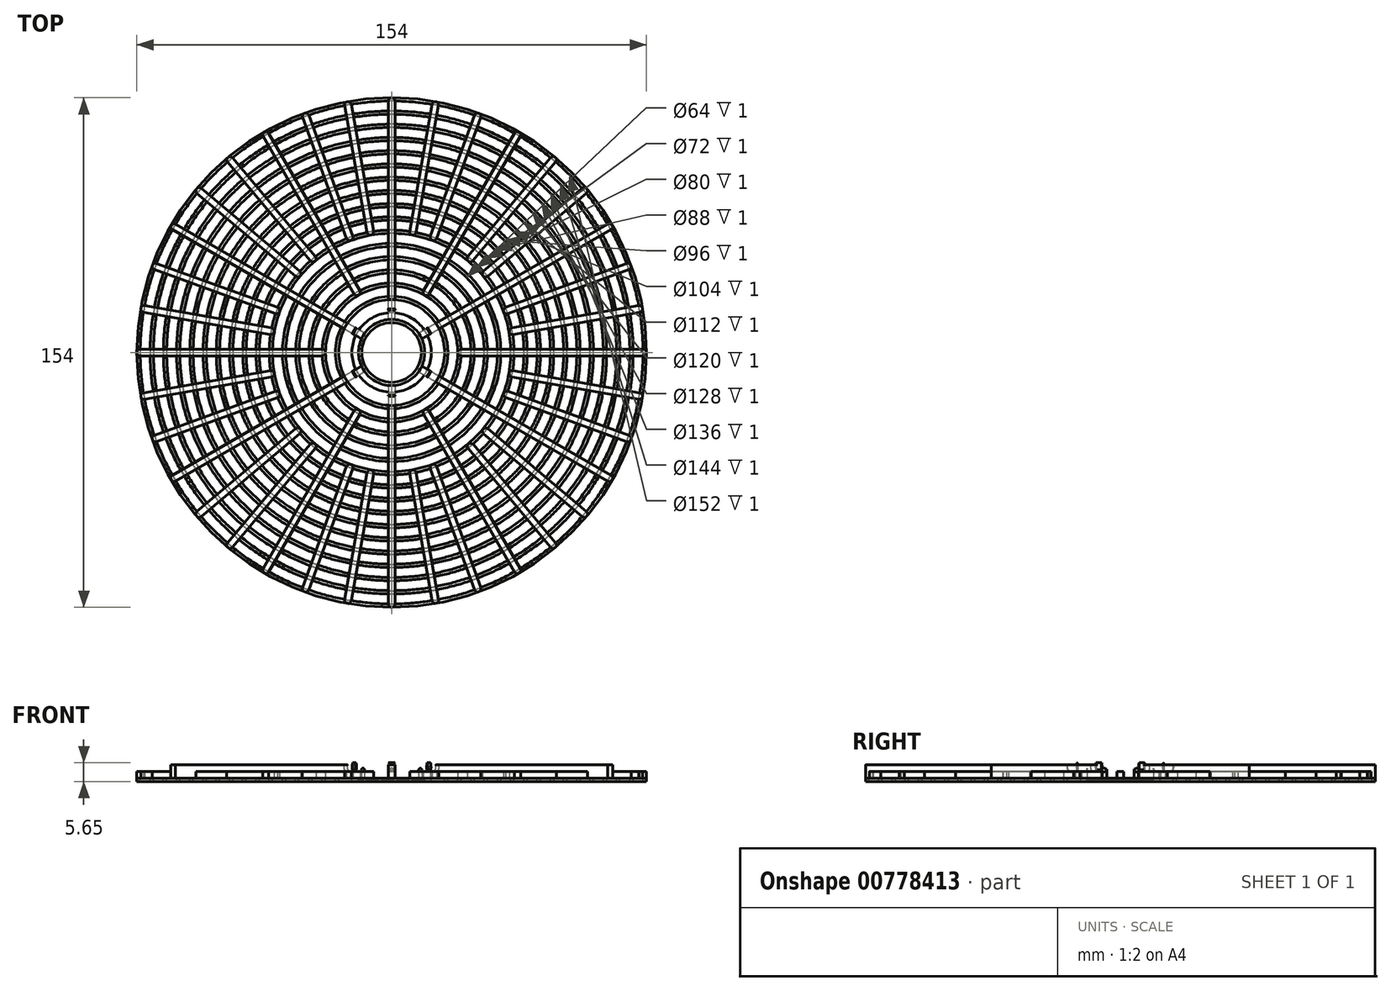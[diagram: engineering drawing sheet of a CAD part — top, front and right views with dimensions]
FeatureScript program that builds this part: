
annotation { "Feature Type Name" : "Feature", "Feature Type Description" : "" }
export const myFeature = defineFeature(function(context is Context, id is Id, definition is map)
    precondition{}
    {
        {
            var Q0;
            Q0=qCreatedBy(makeId("Front.planeOp"),FACE);
            var sketch = newSketch(context, id + "F0", { "sketchPlane" : qUnion([Q0])});
            skLineSegment(sketch, "E0.bottom", {"start": v(16, -1) * mm, "end": v(17, -1) * mm});
            skLineSegment(sketch, "E0.top", {"start": v(16, 0) * mm, "end": v(17, 0) * mm});
            skLineSegment(sketch, "E0.left", {"start": v(16, -1) * mm, "end": v(16, 0) * mm});
            skLineSegment(sketch, "E0.right", {"start": v(17, -1) * mm, "end": v(17, 0) * mm});
            skLineSegment(sketch, "E1.1.0.0", {"start": v(21, -1) * mm, "end": v(21, 0) * mm});
            skLineSegment(sketch, "E1.1.0.1", {"start": v(20, -1) * mm, "end": v(20, 0) * mm});
            skLineSegment(sketch, "E1.1.0.2", {"start": v(20, 0) * mm, "end": v(21, 0) * mm});
            skLineSegment(sketch, "E1.1.0.3", {"start": v(20, -1) * mm, "end": v(21, -1) * mm});
            skLineSegment(sketch, "E1.2.0.0", {"start": v(25, -1) * mm, "end": v(25, 0) * mm});
            skLineSegment(sketch, "E1.2.0.1", {"start": v(24, -1) * mm, "end": v(24, 0) * mm});
            skLineSegment(sketch, "E1.2.0.2", {"start": v(24, 0) * mm, "end": v(25, 0) * mm});
            skLineSegment(sketch, "E1.2.0.3", {"start": v(24, -1) * mm, "end": v(25, -1) * mm});
            skLineSegment(sketch, "E1.3.0.0", {"start": v(29, -1) * mm, "end": v(29, 0) * mm});
            skLineSegment(sketch, "E1.3.0.1", {"start": v(28, -1) * mm, "end": v(28, 0) * mm});
            skLineSegment(sketch, "E1.3.0.2", {"start": v(28, 0) * mm, "end": v(29, 0) * mm});
            skLineSegment(sketch, "E1.3.0.3", {"start": v(28, -1) * mm, "end": v(29, -1) * mm});
            skLineSegment(sketch, "E1.4.0.0", {"start": v(33, -1) * mm, "end": v(33, 0) * mm});
            skLineSegment(sketch, "E1.4.0.1", {"start": v(32, -1) * mm, "end": v(32, 0) * mm});
            skLineSegment(sketch, "E1.4.0.2", {"start": v(32, 0) * mm, "end": v(33, 0) * mm});
            skLineSegment(sketch, "E1.4.0.3", {"start": v(32, -1) * mm, "end": v(33, -1) * mm});
            skLineSegment(sketch, "E1.5.0.0", {"start": v(37, -1) * mm, "end": v(37, 0) * mm});
            skLineSegment(sketch, "E1.5.0.1", {"start": v(36, -1) * mm, "end": v(36, 0) * mm});
            skLineSegment(sketch, "E1.5.0.2", {"start": v(36, 0) * mm, "end": v(37, 0) * mm});
            skLineSegment(sketch, "E1.5.0.3", {"start": v(36, -1) * mm, "end": v(37, -1) * mm});
            skLineSegment(sketch, "E1.6.0.0", {"start": v(41, -1) * mm, "end": v(41, 0) * mm});
            skLineSegment(sketch, "E1.6.0.1", {"start": v(40, -1) * mm, "end": v(40, 0) * mm});
            skLineSegment(sketch, "E1.6.0.2", {"start": v(40, 0) * mm, "end": v(41, 0) * mm});
            skLineSegment(sketch, "E1.6.0.3", {"start": v(40, -1) * mm, "end": v(41, -1) * mm});
            skLineSegment(sketch, "E1.7.0.0", {"start": v(45, -1) * mm, "end": v(45, 0) * mm});
            skLineSegment(sketch, "E1.7.0.1", {"start": v(44, -1) * mm, "end": v(44, 0) * mm});
            skLineSegment(sketch, "E1.7.0.2", {"start": v(44, 0) * mm, "end": v(45, 0) * mm});
            skLineSegment(sketch, "E1.7.0.3", {"start": v(44, -1) * mm, "end": v(45, -1) * mm});
            skLineSegment(sketch, "E1.8.0.0", {"start": v(49, -1) * mm, "end": v(49, 0) * mm});
            skLineSegment(sketch, "E1.8.0.1", {"start": v(48, -1) * mm, "end": v(48, 0) * mm});
            skLineSegment(sketch, "E1.8.0.2", {"start": v(48, 0) * mm, "end": v(49, 0) * mm});
            skLineSegment(sketch, "E1.8.0.3", {"start": v(48, -1) * mm, "end": v(49, -1) * mm});
            skLineSegment(sketch, "E1.9.0.0", {"start": v(53, -1) * mm, "end": v(53, 0) * mm});
            skLineSegment(sketch, "E1.9.0.1", {"start": v(52, -1) * mm, "end": v(52, 0) * mm});
            skLineSegment(sketch, "E1.9.0.2", {"start": v(52, 0) * mm, "end": v(53, 0) * mm});
            skLineSegment(sketch, "E1.9.0.3", {"start": v(52, -1) * mm, "end": v(53, -1) * mm});
            skLineSegment(sketch, "E1.10.0.0", {"start": v(57, -1) * mm, "end": v(57, 0) * mm});
            skLineSegment(sketch, "E1.10.0.1", {"start": v(56, -1) * mm, "end": v(56, 0) * mm});
            skLineSegment(sketch, "E1.10.0.2", {"start": v(56, 0) * mm, "end": v(57, 0) * mm});
            skLineSegment(sketch, "E1.10.0.3", {"start": v(56, -1) * mm, "end": v(57, -1) * mm});
            skLineSegment(sketch, "E1.11.0.0", {"start": v(61, -1) * mm, "end": v(61, 0) * mm});
            skLineSegment(sketch, "E1.11.0.1", {"start": v(60, -1) * mm, "end": v(60, 0) * mm});
            skLineSegment(sketch, "E1.11.0.2", {"start": v(60, 0) * mm, "end": v(61, 0) * mm});
            skLineSegment(sketch, "E1.11.0.3", {"start": v(60, -1) * mm, "end": v(61, -1) * mm});
            skLineSegment(sketch, "E1.12.0.0", {"start": v(65, -1) * mm, "end": v(65, 0) * mm});
            skLineSegment(sketch, "E1.12.0.1", {"start": v(64, -1) * mm, "end": v(64, 0) * mm});
            skLineSegment(sketch, "E1.12.0.2", {"start": v(64, 0) * mm, "end": v(65, 0) * mm});
            skLineSegment(sketch, "E1.12.0.3", {"start": v(64, -1) * mm, "end": v(65, -1) * mm});
            skLineSegment(sketch, "E1.13.0.0", {"start": v(69, -1) * mm, "end": v(69, 0) * mm});
            skLineSegment(sketch, "E1.13.0.1", {"start": v(68, -1) * mm, "end": v(68, 0) * mm});
            skLineSegment(sketch, "E1.13.0.2", {"start": v(68, 0) * mm, "end": v(69, 0) * mm});
            skLineSegment(sketch, "E1.13.0.3", {"start": v(68, -1) * mm, "end": v(69, -1) * mm});
            skLineSegment(sketch, "E1.14.0.0", {"start": v(73, -1) * mm, "end": v(73, 0) * mm});
            skLineSegment(sketch, "E1.14.0.1", {"start": v(72, -1) * mm, "end": v(72, 0) * mm});
            skLineSegment(sketch, "E1.14.0.2", {"start": v(72, 0) * mm, "end": v(73, 0) * mm});
            skLineSegment(sketch, "E1.14.0.3", {"start": v(72, -1) * mm, "end": v(73, -1) * mm});
            skLineSegment(sketch, "E1.15.0.0", {"start": v(77, -1) * mm, "end": v(77, 0) * mm});
            skLineSegment(sketch, "E1.15.0.1", {"start": v(76, -1) * mm, "end": v(76, 0) * mm});
            skLineSegment(sketch, "E1.15.0.2", {"start": v(76, 0) * mm, "end": v(77, 0) * mm});
            skLineSegment(sketch, "E1.15.0.3", {"start": v(76, -1) * mm, "end": v(77, -1) * mm});
            skLineSegment(sketch, "E1.direction1", {"start": v(16, -1) * mm, "end": v(20, -1) * mm, "construction": true});
            skLineSegment(sketch, "E2", {"start": v(0, 44.74) * mm, "end": v(0, -46.31) * mm, "construction": true});
            skLineSegment(sketch, "E3", {"start": v(-40.31, 0) * mm, "end": v(86.53, 0) * mm, "construction": true});
            skLineSegment(sketch, "E4.bottom", {"start": v(0, -1) * mm, "end": v(12, -1) * mm});
            skLineSegment(sketch, "E4.top", {"start": v(0, 0) * mm, "end": v(9, 0) * mm});
            skLineSegment(sketch, "E4.left", {"start": v(0, -1) * mm, "end": v(0, 0) * mm});
            skLineSegment(sketch, "E4.right", {"start": v(12, -1) * mm, "end": v(12, 0) * mm});
            skLineSegment(sketch, "E5.top", {"start": v(9, -0.6) * mm, "end": v(10, -0.6) * mm});
            skLineSegment(sketch, "E5.left", {"start": v(9, 0) * mm, "end": v(9, -0.6) * mm});
            skLineSegment(sketch, "E5.right", {"start": v(10, 0) * mm, "end": v(10, -0.6) * mm});
            skLineSegment(sketch, "E6.trimOffspring", {"start": v(10, 0) * mm, "end": v(12, 0) * mm});
            skSolve(sketch);
        }
        {
            var Q0;
            Q0=makeQuery(id+"F0.imprint","IMPRINT",FACE,{"disambiguationData":[TD([[makeQuery(id+"F0.imprint","IMPRINT",EDGE,{"derivedFrom":sQuery(id+"F0.wireOp",EDGE,"E1.15.0.0")}),1.0]])]});
            var Q1;
            Q1=makeQuery(id+"F0.imprint","IMPRINT",FACE,{"disambiguationData":[TD([[makeQuery(id+"F0.imprint","IMPRINT",EDGE,{"derivedFrom":sQuery(id+"F0.wireOp",EDGE,"E1.13.0.0")}),1.0]])]});
            var Q2;
            Q2=makeQuery(id+"F0.imprint","IMPRINT",FACE,{"disambiguationData":[TD([[makeQuery(id+"F0.imprint","IMPRINT",EDGE,{"derivedFrom":sQuery(id+"F0.wireOp",EDGE,"E1.14.0.0")}),1.0]])]});
            var Q3;
            Q3=makeQuery(id+"F0.imprint","IMPRINT",FACE,{"disambiguationData":[TD([[makeQuery(id+"F0.imprint","IMPRINT",EDGE,{"derivedFrom":sQuery(id+"F0.wireOp",EDGE,"E1.3.0.0")}),1.0]])]});
            var Q4;
            Q4=makeQuery(id+"F0.imprint","IMPRINT",FACE,{"disambiguationData":[TD([[makeQuery(id+"F0.imprint","IMPRINT",EDGE,{"derivedFrom":sQuery(id+"F0.wireOp",EDGE,"E1.4.0.0")}),1.0]])]});
            var Q5;
            Q5=makeQuery(id+"F0.imprint","IMPRINT",FACE,{"disambiguationData":[TD([[makeQuery(id+"F0.imprint","IMPRINT",EDGE,{"derivedFrom":sQuery(id+"F0.wireOp",EDGE,"E1.5.0.0")}),1.0]])]});
            var Q6;
            Q6=makeQuery(id+"F0.imprint","IMPRINT",FACE,{"disambiguationData":[TD([[makeQuery(id+"F0.imprint","IMPRINT",EDGE,{"derivedFrom":sQuery(id+"F0.wireOp",EDGE,"E1.7.0.0")}),1.0]])]});
            var Q7;
            Q7=makeQuery(id+"F0.imprint","IMPRINT",FACE,{"disambiguationData":[TD([[makeQuery(id+"F0.imprint","IMPRINT",EDGE,{"derivedFrom":sQuery(id+"F0.wireOp",EDGE,"E1.6.0.0")}),1.0]])]});
            var Q8;
            Q8=makeQuery(id+"F0.imprint","IMPRINT",FACE,{"disambiguationData":[TD([[makeQuery(id+"F0.imprint","IMPRINT",EDGE,{"derivedFrom":sQuery(id+"F0.wireOp",EDGE,"E1.2.0.0")}),1.0]])]});
            var Q9;
            Q9=makeQuery(id+"F0.imprint","IMPRINT",FACE,{"disambiguationData":[TD([[makeQuery(id+"F0.imprint","IMPRINT",EDGE,{"derivedFrom":sQuery(id+"F0.wireOp",EDGE,"E1.8.0.0")}),1.0]])]});
            var Q10;
            Q10=makeQuery(id+"F0.imprint","IMPRINT",FACE,{"disambiguationData":[TD([[makeQuery(id+"F0.imprint","IMPRINT",EDGE,{"derivedFrom":sQuery(id+"F0.wireOp",EDGE,"E1.9.0.0")}),1.0]])]});
            var Q11;
            Q11=makeQuery(id+"F0.imprint","IMPRINT",FACE,{"disambiguationData":[TD([[makeQuery(id+"F0.imprint","IMPRINT",EDGE,{"derivedFrom":sQuery(id+"F0.wireOp",EDGE,"E1.10.0.0")}),1.0]])]});
            var Q12;
            Q12=makeQuery(id+"F0.imprint","IMPRINT",FACE,{"disambiguationData":[TD([[makeQuery(id+"F0.imprint","IMPRINT",EDGE,{"derivedFrom":sQuery(id+"F0.wireOp",EDGE,"E1.11.0.0")}),1.0]])]});
            var Q13;
            Q13=makeQuery(id+"F0.imprint","IMPRINT",FACE,{"disambiguationData":[TD([[makeQuery(id+"F0.imprint","IMPRINT",EDGE,{"derivedFrom":sQuery(id+"F0.wireOp",EDGE,"E1.12.0.0")}),1.0]])]});
            var Q14;
            Q14=makeQuery(id+"F0.imprint","IMPRINT",FACE,{"disambiguationData":[TD([[makeQuery(id+"F0.imprint","IMPRINT",EDGE,{"derivedFrom":sQuery(id+"F0.wireOp",EDGE,"E0.bottom")}),1.0]])]});
            var Q15;
            Q15=makeQuery(id+"F0.imprint","IMPRINT",FACE,{"disambiguationData":[TD([[makeQuery(id+"F0.imprint","IMPRINT",EDGE,{"derivedFrom":sQuery(id+"F0.wireOp",EDGE,"E1.1.0.0")}),1.0]])]});
            var Q16;
            Q16=makeQuery(id+"F0.imprint","IMPRINT",FACE,{"disambiguationData":[TD([[makeQuery(id+"F0.imprint","IMPRINT",EDGE,{"derivedFrom":sQuery(id+"F0.wireOp",EDGE,"E4.bottom")}),1.0]])]});
            var Q17;
            Q17=sQuery(id+"F0.wireOp",EDGE,"E2");
            revolve(context, id + "F1", {"surfaceOperationType" : NewSurfaceOperationType.NEW, "entities" : qUnion([Q0, Q1, Q2, Q3, Q4, Q5, Q6, Q7, Q8, Q9, Q10, Q11, Q12, Q13, Q14, Q15, Q16]), "axis" : qUnion([Q17]), "revolveType" : RevolveType.FULL});
        }
        {
            var Q0;
            Q0=qCreatedBy(makeId("Top.planeOp"),FACE);
            var sketch = newSketch(context, id + "F2", { "sketchPlane" : qUnion([Q0])});
            skLineSegment(sketch, "E7.top", {"start": v(1, -10) * mm, "end": v(-1, -10) * mm});
            skLineSegment(sketch, "E7.left", {"start": v(1, -76) * mm, "end": v(1, -10) * mm});
            skLineSegment(sketch, "E7.right", {"start": v(-1, -76) * mm, "end": v(-1, -10) * mm});
            skPoint(sketch, "E7.middle", {"position": v(0, -28.84) * mm});
            skArc(sketch, "E8", {"start": v(-1, -76) * mm, "mid": v(0, -77) * mm, "end": v(1, -76) * mm});
            skLineSegment(sketch, "E9.1.0", {"start": v(65.32, -38.87) * mm, "end": v(8.16, -5.87) * mm});
            skLineSegment(sketch, "E9.1.1", {"start": v(66.32, -37.13) * mm, "end": v(9.16, -4.13) * mm});
            skPoint(sketch, "E9.1.2", {"position": v(24.97, -14.42) * mm});
            skLineSegment(sketch, "E9.1.3", {"start": v(9.16, -4.13) * mm, "end": v(8.16, -5.87) * mm});
            skArc(sketch, "E9.1.4", {"start": v(65.32, -38.87) * mm, "mid": v(66.68, -38.5) * mm, "end": v(66.32, -37.13) * mm});
            skLineSegment(sketch, "E9.2.0", {"start": v(66.32, 37.13) * mm, "end": v(9.16, 4.13) * mm});
            skLineSegment(sketch, "E9.2.1", {"start": v(65.32, 38.87) * mm, "end": v(8.16, 5.87) * mm});
            skPoint(sketch, "E9.2.2", {"position": v(24.97, 14.42) * mm});
            skLineSegment(sketch, "E9.2.3", {"start": v(8.16, 5.87) * mm, "end": v(9.16, 4.13) * mm});
            skArc(sketch, "E9.2.4", {"start": v(66.32, 37.13) * mm, "mid": v(66.68, 38.5) * mm, "end": v(65.32, 38.87) * mm});
            skLineSegment(sketch, "E9.3.0", {"start": v(1, 76) * mm, "end": v(1, 10) * mm});
            skLineSegment(sketch, "E9.3.1", {"start": v(-1, 76) * mm, "end": v(-1, 10) * mm});
            skPoint(sketch, "E9.3.2", {"position": v(0, 28.84) * mm});
            skLineSegment(sketch, "E9.3.3", {"start": v(-1, 10) * mm, "end": v(1, 10) * mm});
            skArc(sketch, "E9.3.4", {"start": v(1, 76) * mm, "mid": v(0, 77) * mm, "end": v(-1, 76) * mm});
            skPoint(sketch, "E9.center", {"position": v(0, 0) * mm});
            skLineSegment(sketch, "E10.1.4.0", {"start": v(-65.32, 38.87) * mm, "end": v(-8.16, 5.87) * mm});
            skLineSegment(sketch, "E10.3.4.0", {"start": v(-66.32, 37.13) * mm, "end": v(-9.16, 4.13) * mm});
            skPoint(sketch, "E10.6.4.0", {"position": v(-24.97, 14.42) * mm});
            skLineSegment(sketch, "E10.7.4.0", {"start": v(-9.16, 4.13) * mm, "end": v(-8.16, 5.87) * mm});
            skArc(sketch, "E10.10.4.0", {"start": v(-65.32, 38.87) * mm, "mid": v(-66.68, 38.5) * mm, "end": v(-66.32, 37.13) * mm});
            skLineSegment(sketch, "E10.1.5.0", {"start": v(-66.32, -37.13) * mm, "end": v(-9.16, -4.13) * mm});
            skLineSegment(sketch, "E10.3.5.0", {"start": v(-65.32, -38.87) * mm, "end": v(-8.16, -5.87) * mm});
            skPoint(sketch, "E10.6.5.0", {"position": v(-24.97, -14.42) * mm});
            skLineSegment(sketch, "E10.7.5.0", {"start": v(-8.16, -5.87) * mm, "end": v(-9.16, -4.13) * mm});
            skArc(sketch, "E10.10.5.0", {"start": v(-66.32, -37.13) * mm, "mid": v(-66.68, -38.5) * mm, "end": v(-65.32, -38.87) * mm});
            skSolve(sketch);
        }
        {
            var Q0;
            Q0 = qSketchRegion(id + "F2", true);
            extrude(context, id + "F3", {"entities" : qUnion([Q0]), "depth" : 4 * mm, "offsetDistance" : 25 * mm});
        }
        {
            var Q0;
            Q0=qCreatedBy(makeId("Top.planeOp"),FACE);
            var sketch = newSketch(context, id + "F4", { "sketchPlane" : qUnion([Q0])});
            skArc(sketch, "E11", {"start": v(-76, 1) * mm, "mid": v(-77, 0) * mm, "end": v(-76, -1) * mm});
            skArc(sketch, "E12", {"start": v(-21.01, -1) * mm, "mid": v(-20.01, 0) * mm, "end": v(-21.01, 1) * mm});
            skLineSegment(sketch, "E13", {"start": v(-76, -1) * mm, "end": v(-21.01, -1) * mm});
            skLineSegment(sketch, "E14", {"start": v(-21.01, 1) * mm, "end": v(-76, 1) * mm});
            skArc(sketch, "E15.1.0", {"start": v(-38.86, -65.3) * mm, "mid": v(-38.5, -66.68) * mm, "end": v(-37.13, -66.3) * mm});
            skLineSegment(sketch, "E15.1.1", {"start": v(-37.13, -66.3) * mm, "end": v(-9.64, -18.7) * mm});
            skLineSegment(sketch, "E15.1.2", {"start": v(-11.37, -17.7) * mm, "end": v(-38.86, -65.3) * mm});
            skArc(sketch, "E15.1.3", {"start": v(-9.64, -18.7) * mm, "mid": v(-10, -17.33) * mm, "end": v(-11.37, -17.7) * mm});
            skArc(sketch, "E15.2.0", {"start": v(37.13, -66.3) * mm, "mid": v(38.5, -66.68) * mm, "end": v(38.86, -65.3) * mm});
            skLineSegment(sketch, "E15.2.1", {"start": v(38.86, -65.3) * mm, "end": v(11.37, -17.7) * mm});
            skLineSegment(sketch, "E15.2.2", {"start": v(9.64, -18.7) * mm, "end": v(37.13, -66.3) * mm});
            skArc(sketch, "E15.2.3", {"start": v(11.37, -17.7) * mm, "mid": v(10, -17.33) * mm, "end": v(9.64, -18.7) * mm});
            skArc(sketch, "E15.3.0", {"start": v(76, -1) * mm, "mid": v(77, 0) * mm, "end": v(76, 1) * mm});
            skLineSegment(sketch, "E15.3.1", {"start": v(76, 1) * mm, "end": v(21.01, 1) * mm});
            skLineSegment(sketch, "E15.3.2", {"start": v(21.01, -1) * mm, "end": v(76, -1) * mm});
            skArc(sketch, "E15.3.3", {"start": v(21.01, 1) * mm, "mid": v(20.01, 0) * mm, "end": v(21.01, -1) * mm});
            skArc(sketch, "E15.4.0", {"start": v(38.86, 65.3) * mm, "mid": v(38.5, 66.68) * mm, "end": v(37.13, 66.3) * mm});
            skLineSegment(sketch, "E15.4.1", {"start": v(37.13, 66.3) * mm, "end": v(9.64, 18.7) * mm});
            skLineSegment(sketch, "E15.4.2", {"start": v(11.37, 17.7) * mm, "end": v(38.86, 65.3) * mm});
            skArc(sketch, "E15.4.3", {"start": v(9.64, 18.7) * mm, "mid": v(10, 17.33) * mm, "end": v(11.37, 17.7) * mm});
            skArc(sketch, "E15.5.0", {"start": v(-37.13, 66.3) * mm, "mid": v(-38.5, 66.68) * mm, "end": v(-38.86, 65.3) * mm});
            skLineSegment(sketch, "E15.5.1", {"start": v(-38.86, 65.3) * mm, "end": v(-11.37, 17.7) * mm});
            skLineSegment(sketch, "E15.5.2", {"start": v(-9.64, 18.7) * mm, "end": v(-37.13, 66.3) * mm});
            skArc(sketch, "E15.5.3", {"start": v(-11.37, 17.7) * mm, "mid": v(-10, 17.33) * mm, "end": v(-9.64, 18.7) * mm});
            skPoint(sketch, "E15.center", {"position": v(0, 0) * mm});
            skSolve(sketch);
        }
        {
            var Q0;
            Q0 = qSketchRegion(id + "F4", true);
            extrude(context, id + "F5", {"entities" : qUnion([Q0]), "operationType" : NewBodyOperationType.ADD, "depth" : 2 * mm, "offsetDistance" : 25 * mm});
        }
        {
            var Q0;
            Q0=qCreatedBy(makeId("Top.planeOp"),FACE);
            var sketch = newSketch(context, id + "F6", { "sketchPlane" : qUnion([Q0])});
            skLineSegment(sketch, "E16", {"start": v(0, 0) * mm, "end": v(-85.94, -31.28) * mm, "construction": true});
            skLineSegment(sketch, "E17", {"start": v(0, 0) * mm, "end": v(-88.81, -15.66) * mm, "construction": true});
            skSolve(sketch);
        }
        {
            var Q0;
            Q0=qCreatedBy(makeId("Top.planeOp"),FACE);
            var sketch = newSketch(context, id + "F7", { "sketchPlane" : qUnion([Q0])});
            skArc(sketch, "E18", {"start": v(-74.99, -12.2) * mm, "mid": v(-75.8, -13.37) * mm, "end": v(-74.64, -14.18) * mm});
            skArc(sketch, "E19", {"start": v(-71.73, -25.04) * mm, "mid": v(-72.33, -26.33) * mm, "end": v(-71.05, -26.92) * mm});
            skArc(sketch, "E20", {"start": v(-34.5, -13.62) * mm, "mid": v(-33.91, -12.34) * mm, "end": v(-35.2, -11.74) * mm});
            skArc(sketch, "E21", {"start": v(-36.36, -7.43) * mm, "mid": v(-35.55, -6.27) * mm, "end": v(-36.7, -5.46) * mm});
            skLineSegment(sketch, "E22", {"start": v(-71.05, -26.92) * mm, "end": v(-34.5, -13.62) * mm});
            skLineSegment(sketch, "E23", {"start": v(-35.2, -11.74) * mm, "end": v(-71.73, -25.04) * mm});
            skLineSegment(sketch, "E24", {"start": v(-74.64, -14.18) * mm, "end": v(-36.36, -7.43) * mm});
            skLineSegment(sketch, "E25", {"start": v(-36.7, -5.46) * mm, "end": v(-74.99, -12.2) * mm});
            skLineSegment(sketch, "E26.1.0", {"start": v(-29.06, -23.08) * mm, "end": v(-58.84, -48.07) * mm});
            skArc(sketch, "E26.1.1", {"start": v(-58.84, -48.07) * mm, "mid": v(-58.96, -49.47) * mm, "end": v(-57.55, -49.6) * mm});
            skLineSegment(sketch, "E26.1.2", {"start": v(-57.55, -49.6) * mm, "end": v(-27.78, -24.61) * mm});
            skLineSegment(sketch, "E26.1.3", {"start": v(-24.6, -27.77) * mm, "end": v(-49.6, -57.56) * mm});
            skLineSegment(sketch, "E26.1.4", {"start": v(-48.07, -58.84) * mm, "end": v(-23.07, -29.05) * mm});
            skArc(sketch, "E26.1.5", {"start": v(-49.6, -57.56) * mm, "mid": v(-49.48, -58.97) * mm, "end": v(-48.07, -58.84) * mm});
            skArc(sketch, "E26.1.6", {"start": v(-27.78, -24.61) * mm, "mid": v(-27.65, -23.2) * mm, "end": v(-29.06, -23.08) * mm});
            skArc(sketch, "E26.1.7", {"start": v(-23.07, -29.05) * mm, "mid": v(-23.2, -27.64) * mm, "end": v(-24.6, -27.77) * mm});
            skLineSegment(sketch, "E26.2.0", {"start": v(-13.63, -34.52) * mm, "end": v(-26.92, -71.04) * mm});
            skArc(sketch, "E26.2.1", {"start": v(-26.92, -71.04) * mm, "mid": v(-26.32, -72.33) * mm, "end": v(-25.04, -71.73) * mm});
            skLineSegment(sketch, "E26.2.2", {"start": v(-25.04, -71.73) * mm, "end": v(-11.75, -35.2) * mm});
            skLineSegment(sketch, "E26.2.3", {"start": v(-7.42, -36.35) * mm, "end": v(-14.18, -74.65) * mm});
            skLineSegment(sketch, "E26.2.4", {"start": v(-12.2, -75) * mm, "end": v(-5.46, -36.7) * mm});
            skArc(sketch, "E26.2.5", {"start": v(-14.18, -74.65) * mm, "mid": v(-13.37, -75.8) * mm, "end": v(-12.2, -75) * mm});
            skArc(sketch, "E26.2.6", {"start": v(-11.75, -35.2) * mm, "mid": v(-12.35, -33.92) * mm, "end": v(-13.63, -34.52) * mm});
            skArc(sketch, "E26.2.7", {"start": v(-5.46, -36.7) * mm, "mid": v(-6.27, -35.54) * mm, "end": v(-7.42, -36.35) * mm});
            skLineSegment(sketch, "E26.3.0", {"start": v(5.46, -36.7) * mm, "end": v(12.2, -74.99) * mm});
            skArc(sketch, "E26.3.1", {"start": v(12.2, -74.99) * mm, "mid": v(13.37, -75.8) * mm, "end": v(14.18, -74.64) * mm});
            skLineSegment(sketch, "E26.3.2", {"start": v(14.18, -74.64) * mm, "end": v(7.43, -36.36) * mm});
            skLineSegment(sketch, "E26.3.3", {"start": v(11.74, -35.2) * mm, "end": v(25.04, -71.73) * mm});
            skLineSegment(sketch, "E26.3.4", {"start": v(26.92, -71.05) * mm, "end": v(13.62, -34.5) * mm});
            skArc(sketch, "E26.3.5", {"start": v(25.04, -71.73) * mm, "mid": v(26.33, -72.33) * mm, "end": v(26.92, -71.05) * mm});
            skArc(sketch, "E26.3.6", {"start": v(7.43, -36.36) * mm, "mid": v(6.27, -35.55) * mm, "end": v(5.46, -36.7) * mm});
            skArc(sketch, "E26.3.7", {"start": v(13.62, -34.5) * mm, "mid": v(12.34, -33.91) * mm, "end": v(11.74, -35.2) * mm});
            skLineSegment(sketch, "E26.4.0", {"start": v(23.08, -29.06) * mm, "end": v(48.07, -58.84) * mm});
            skArc(sketch, "E26.4.1", {"start": v(48.07, -58.84) * mm, "mid": v(49.47, -58.96) * mm, "end": v(49.6, -57.55) * mm});
            skLineSegment(sketch, "E26.4.2", {"start": v(49.6, -57.55) * mm, "end": v(24.61, -27.78) * mm});
            skLineSegment(sketch, "E26.4.3", {"start": v(27.77, -24.6) * mm, "end": v(57.56, -49.6) * mm});
            skLineSegment(sketch, "E26.4.4", {"start": v(58.84, -48.07) * mm, "end": v(29.05, -23.07) * mm});
            skArc(sketch, "E26.4.5", {"start": v(57.56, -49.6) * mm, "mid": v(58.97, -49.48) * mm, "end": v(58.84, -48.07) * mm});
            skArc(sketch, "E26.4.6", {"start": v(24.61, -27.78) * mm, "mid": v(23.2, -27.65) * mm, "end": v(23.08, -29.06) * mm});
            skArc(sketch, "E26.4.7", {"start": v(29.05, -23.07) * mm, "mid": v(27.64, -23.2) * mm, "end": v(27.77, -24.6) * mm});
            skLineSegment(sketch, "E26.5.0", {"start": v(34.52, -13.63) * mm, "end": v(71.04, -26.92) * mm});
            skArc(sketch, "E26.5.1", {"start": v(71.04, -26.92) * mm, "mid": v(72.33, -26.32) * mm, "end": v(71.73, -25.04) * mm});
            skLineSegment(sketch, "E26.5.2", {"start": v(71.73, -25.04) * mm, "end": v(35.2, -11.75) * mm});
            skLineSegment(sketch, "E26.5.3", {"start": v(36.35, -7.42) * mm, "end": v(74.65, -14.18) * mm});
            skLineSegment(sketch, "E26.5.4", {"start": v(75, -12.2) * mm, "end": v(36.7, -5.46) * mm});
            skArc(sketch, "E26.5.5", {"start": v(74.65, -14.18) * mm, "mid": v(75.8, -13.37) * mm, "end": v(75, -12.2) * mm});
            skArc(sketch, "E26.5.6", {"start": v(35.2, -11.75) * mm, "mid": v(33.92, -12.35) * mm, "end": v(34.52, -13.63) * mm});
            skArc(sketch, "E26.5.7", {"start": v(36.7, -5.46) * mm, "mid": v(35.54, -6.27) * mm, "end": v(36.35, -7.42) * mm});
            skLineSegment(sketch, "E26.6.0", {"start": v(36.7, 5.46) * mm, "end": v(74.99, 12.2) * mm});
            skArc(sketch, "E26.6.1", {"start": v(74.99, 12.2) * mm, "mid": v(75.8, 13.37) * mm, "end": v(74.64, 14.18) * mm});
            skLineSegment(sketch, "E26.6.2", {"start": v(74.64, 14.18) * mm, "end": v(36.36, 7.43) * mm});
            skLineSegment(sketch, "E26.6.3", {"start": v(35.2, 11.74) * mm, "end": v(71.73, 25.04) * mm});
            skLineSegment(sketch, "E26.6.4", {"start": v(71.05, 26.92) * mm, "end": v(34.5, 13.62) * mm});
            skArc(sketch, "E26.6.5", {"start": v(71.73, 25.04) * mm, "mid": v(72.33, 26.33) * mm, "end": v(71.05, 26.92) * mm});
            skArc(sketch, "E26.6.6", {"start": v(36.36, 7.43) * mm, "mid": v(35.55, 6.27) * mm, "end": v(36.7, 5.46) * mm});
            skArc(sketch, "E26.6.7", {"start": v(34.5, 13.62) * mm, "mid": v(33.91, 12.34) * mm, "end": v(35.2, 11.74) * mm});
            skLineSegment(sketch, "E26.7.0", {"start": v(29.06, 23.08) * mm, "end": v(58.84, 48.07) * mm});
            skArc(sketch, "E26.7.1", {"start": v(58.84, 48.07) * mm, "mid": v(58.96, 49.47) * mm, "end": v(57.55, 49.6) * mm});
            skLineSegment(sketch, "E26.7.2", {"start": v(57.55, 49.6) * mm, "end": v(27.78, 24.61) * mm});
            skLineSegment(sketch, "E26.7.3", {"start": v(24.6, 27.77) * mm, "end": v(49.6, 57.56) * mm});
            skLineSegment(sketch, "E26.7.4", {"start": v(48.07, 58.84) * mm, "end": v(23.07, 29.05) * mm});
            skArc(sketch, "E26.7.5", {"start": v(49.6, 57.56) * mm, "mid": v(49.48, 58.97) * mm, "end": v(48.07, 58.84) * mm});
            skArc(sketch, "E26.7.6", {"start": v(27.78, 24.61) * mm, "mid": v(27.65, 23.2) * mm, "end": v(29.06, 23.08) * mm});
            skArc(sketch, "E26.7.7", {"start": v(23.07, 29.05) * mm, "mid": v(23.2, 27.64) * mm, "end": v(24.6, 27.77) * mm});
            skLineSegment(sketch, "E26.8.0", {"start": v(13.63, 34.52) * mm, "end": v(26.92, 71.04) * mm});
            skArc(sketch, "E26.8.1", {"start": v(26.92, 71.04) * mm, "mid": v(26.32, 72.33) * mm, "end": v(25.04, 71.73) * mm});
            skLineSegment(sketch, "E26.8.2", {"start": v(25.04, 71.73) * mm, "end": v(11.75, 35.2) * mm});
            skLineSegment(sketch, "E26.8.3", {"start": v(7.42, 36.35) * mm, "end": v(14.18, 74.65) * mm});
            skLineSegment(sketch, "E26.8.4", {"start": v(12.2, 75) * mm, "end": v(5.46, 36.7) * mm});
            skArc(sketch, "E26.8.5", {"start": v(14.18, 74.65) * mm, "mid": v(13.37, 75.8) * mm, "end": v(12.2, 75) * mm});
            skArc(sketch, "E26.8.6", {"start": v(11.75, 35.2) * mm, "mid": v(12.35, 33.92) * mm, "end": v(13.63, 34.52) * mm});
            skArc(sketch, "E26.8.7", {"start": v(5.46, 36.7) * mm, "mid": v(6.27, 35.54) * mm, "end": v(7.42, 36.35) * mm});
            skLineSegment(sketch, "E26.9.0", {"start": v(-5.46, 36.7) * mm, "end": v(-12.2, 74.99) * mm});
            skArc(sketch, "E26.9.1", {"start": v(-12.2, 74.99) * mm, "mid": v(-13.37, 75.8) * mm, "end": v(-14.18, 74.64) * mm});
            skLineSegment(sketch, "E26.9.2", {"start": v(-14.18, 74.64) * mm, "end": v(-7.43, 36.36) * mm});
            skLineSegment(sketch, "E26.9.3", {"start": v(-11.74, 35.2) * mm, "end": v(-25.04, 71.73) * mm});
            skLineSegment(sketch, "E26.9.4", {"start": v(-26.92, 71.05) * mm, "end": v(-13.62, 34.5) * mm});
            skArc(sketch, "E26.9.5", {"start": v(-25.04, 71.73) * mm, "mid": v(-26.33, 72.33) * mm, "end": v(-26.92, 71.05) * mm});
            skArc(sketch, "E26.9.6", {"start": v(-7.43, 36.36) * mm, "mid": v(-6.27, 35.55) * mm, "end": v(-5.46, 36.7) * mm});
            skArc(sketch, "E26.9.7", {"start": v(-13.62, 34.5) * mm, "mid": v(-12.34, 33.91) * mm, "end": v(-11.74, 35.2) * mm});
            skLineSegment(sketch, "E26.10.0", {"start": v(-23.08, 29.06) * mm, "end": v(-48.07, 58.84) * mm});
            skArc(sketch, "E26.10.1", {"start": v(-48.07, 58.84) * mm, "mid": v(-49.47, 58.96) * mm, "end": v(-49.6, 57.55) * mm});
            skLineSegment(sketch, "E26.10.2", {"start": v(-49.6, 57.55) * mm, "end": v(-24.61, 27.78) * mm});
            skLineSegment(sketch, "E26.10.3", {"start": v(-27.77, 24.6) * mm, "end": v(-57.56, 49.6) * mm});
            skLineSegment(sketch, "E26.10.4", {"start": v(-58.84, 48.07) * mm, "end": v(-29.05, 23.07) * mm});
            skArc(sketch, "E26.10.5", {"start": v(-57.56, 49.6) * mm, "mid": v(-58.97, 49.48) * mm, "end": v(-58.84, 48.07) * mm});
            skArc(sketch, "E26.10.6", {"start": v(-24.61, 27.78) * mm, "mid": v(-23.2, 27.65) * mm, "end": v(-23.08, 29.06) * mm});
            skArc(sketch, "E26.10.7", {"start": v(-29.05, 23.07) * mm, "mid": v(-27.64, 23.2) * mm, "end": v(-27.77, 24.6) * mm});
            skLineSegment(sketch, "E26.11.0", {"start": v(-34.52, 13.63) * mm, "end": v(-71.04, 26.92) * mm});
            skArc(sketch, "E26.11.1", {"start": v(-71.04, 26.92) * mm, "mid": v(-72.33, 26.32) * mm, "end": v(-71.73, 25.04) * mm});
            skLineSegment(sketch, "E26.11.2", {"start": v(-71.73, 25.04) * mm, "end": v(-35.2, 11.75) * mm});
            skLineSegment(sketch, "E26.11.3", {"start": v(-36.35, 7.42) * mm, "end": v(-74.65, 14.18) * mm});
            skLineSegment(sketch, "E26.11.4", {"start": v(-75, 12.2) * mm, "end": v(-36.7, 5.46) * mm});
            skArc(sketch, "E26.11.5", {"start": v(-74.65, 14.18) * mm, "mid": v(-75.8, 13.37) * mm, "end": v(-75, 12.2) * mm});
            skArc(sketch, "E26.11.6", {"start": v(-35.2, 11.75) * mm, "mid": v(-33.92, 12.35) * mm, "end": v(-34.52, 13.63) * mm});
            skArc(sketch, "E26.11.7", {"start": v(-36.7, 5.46) * mm, "mid": v(-35.54, 6.27) * mm, "end": v(-36.35, 7.42) * mm});
            skPoint(sketch, "E26.center", {"position": v(0, 0) * mm});
            skSolve(sketch);
        }
        {
            var Q0;
            Q0 = qSketchRegion(id + "F7", true);
            extrude(context, id + "F8", {"entities" : qUnion([Q0]), "operationType" : NewBodyOperationType.ADD, "depth" : 2 * mm, "offsetDistance" : 25 * mm});
        }
        {
            var Q0;
            Q0=makeQuery(id+"F3.opExtrude","CAP_FACE",FACE,{"disambiguationData":[OSD([sQuery(id+"F2.wireOp",EDGE,"E9.3.0"),sQuery(id+"F2.wireOp",EDGE,"E9.3.1"),sQuery(id+"F2.wireOp",EDGE,"E9.3.3"),sQuery(id+"F2.wireOp",EDGE,"E9.3.4")])],"isStart":false});
            var sketch = newSketch(context, id + "F9", { "sketchPlane" : qUnion([Q0])});
            skLineSegment(sketch, "E27.bottom", {"start": v(-1, 10) * mm, "end": v(1, 10) * mm});
            skLineSegment(sketch, "E27.top", {"start": v(-1, 14) * mm, "end": v(1, 14) * mm});
            skLineSegment(sketch, "E27.left", {"start": v(-1, 10) * mm, "end": v(-1, 14) * mm});
            skLineSegment(sketch, "E27.right", {"start": v(1, 10) * mm, "end": v(1, 14) * mm});
            skLineSegment(sketch, "E28.1.0", {"start": v(-12.62, 6.13) * mm, "end": v(-11.62, 7.87) * mm});
            skLineSegment(sketch, "E28.1.1", {"start": v(-9.16, 4.13) * mm, "end": v(-12.62, 6.13) * mm});
            skLineSegment(sketch, "E28.1.2", {"start": v(-9.16, 4.13) * mm, "end": v(-8.16, 5.87) * mm});
            skLineSegment(sketch, "E28.1.3", {"start": v(-8.16, 5.87) * mm, "end": v(-11.62, 7.87) * mm});
            skLineSegment(sketch, "E28.2.0", {"start": v(-11.62, -7.87) * mm, "end": v(-12.62, -6.13) * mm});
            skLineSegment(sketch, "E28.2.1", {"start": v(-8.16, -5.87) * mm, "end": v(-11.62, -7.87) * mm});
            skLineSegment(sketch, "E28.2.2", {"start": v(-8.16, -5.87) * mm, "end": v(-9.16, -4.13) * mm});
            skLineSegment(sketch, "E28.2.3", {"start": v(-9.16, -4.13) * mm, "end": v(-12.62, -6.13) * mm});
            skLineSegment(sketch, "E28.3.0", {"start": v(1, -14) * mm, "end": v(-1, -14) * mm});
            skLineSegment(sketch, "E28.3.1", {"start": v(1, -10) * mm, "end": v(1, -14) * mm});
            skLineSegment(sketch, "E28.3.2", {"start": v(1, -10) * mm, "end": v(-1, -10) * mm});
            skLineSegment(sketch, "E28.3.3", {"start": v(-1, -10) * mm, "end": v(-1, -14) * mm});
            skLineSegment(sketch, "E28.4.0", {"start": v(12.62, -6.13) * mm, "end": v(11.62, -7.87) * mm});
            skLineSegment(sketch, "E28.4.1", {"start": v(9.16, -4.13) * mm, "end": v(12.62, -6.13) * mm});
            skLineSegment(sketch, "E28.4.2", {"start": v(9.16, -4.13) * mm, "end": v(8.16, -5.87) * mm});
            skLineSegment(sketch, "E28.4.3", {"start": v(8.16, -5.87) * mm, "end": v(11.62, -7.87) * mm});
            skLineSegment(sketch, "E28.5.0", {"start": v(11.62, 7.87) * mm, "end": v(12.62, 6.13) * mm});
            skLineSegment(sketch, "E28.5.1", {"start": v(8.16, 5.87) * mm, "end": v(11.62, 7.87) * mm});
            skLineSegment(sketch, "E28.5.2", {"start": v(8.16, 5.87) * mm, "end": v(9.16, 4.13) * mm});
            skLineSegment(sketch, "E28.5.3", {"start": v(9.16, 4.13) * mm, "end": v(12.62, 6.13) * mm});
            skPoint(sketch, "E28.center", {"position": v(0, 0) * mm});
            skSolve(sketch);
        }
        {
            var Q0;
            Q0 = qSketchRegion(id + "F9", true);
            extrude(context, id + "F10", {"entities" : qUnion([Q0]), "operationType" : NewBodyOperationType.ADD, "depth" : 2 * mm, "offsetDistance" : 25 * mm});
        }
        {
            var Q0;
            Q0=qCreatedBy(makeId("Right.planeOp"),FACE);
            var sketch = newSketch(context, id + "F11", { "sketchPlane" : qUnion([Q0])});
            skFitSpline(sketch, "E29", {"points": [v(13.65, 6) * mm, v(13, 4.42) * mm, v(12.85, 3.25) * mm, v(13.21, 2.34) * mm, v(15.55, 2.19) * mm, v(16, 4.02) * mm, v(15.12, 6.23) * mm, v(13.65, 6) * mm]});
            skLineSegment(sketch, "E30", {"start": v(13.21, 2.34) * mm, "end": v(14.43, 2.34) * mm});
            skLineSegment(sketch, "E31", {"start": v(12.85, 3.25) * mm, "end": v(12.85, 2.34) * mm});
            skLineSegment(sketch, "E32", {"start": v(12.85, 2.34) * mm, "end": v(13.21, 2.34) * mm});
            skArc(sketch, "E33", {"start": v(13.22, 5.32) * mm, "mid": v(13.17, 5.78) * mm, "end": v(12.76, 6) * mm});
            skArc(sketch, "E34", {"start": v(11.16, 6) * mm, "mid": v(10.95, 5.96) * mm, "end": v(10.79, 5.83) * mm});
            skLineSegment(sketch, "E35", {"start": v(10, 3.18) * mm, "end": v(10, 2.34) * mm});
            skFitSpline(sketch, "E36.trimOffspring", {"points": [v(10.9, 5.95) * mm, v(10.16, 4.3) * mm, v(10, 3.15) * mm, v(10.37, 2.21) * mm, v(12.72, 2.06) * mm, v(13.17, 3.89) * mm, v(12.28, 6.1) * mm, v(10.9, 5.95) * mm]});
            skLineSegment(sketch, "E37", {"start": v(11.16, 6) * mm, "end": v(12.76, 6) * mm});
            skLineSegment(sketch, "E38", {"start": v(10, 2.34) * mm, "end": v(9.6, 2.34) * mm});
            skLineSegment(sketch, "E39", {"start": v(9.6, 2.34) * mm, "end": v(9.6, 6.82) * mm});
            skLineSegment(sketch, "E40", {"start": v(9.6, 6.82) * mm, "end": v(14.43, 6.83) * mm});
            skPoint(sketch, "E41.endSnap0", {"position": v(14.82, 2.34) * mm});
            skLineSegment(sketch, "E42.trimOffspring", {"start": v(12.45, 2.34) * mm, "end": v(6.98, 2.34) * mm, "construction": true});
            skPoint(sketch, "E43.end.orphan", {"position": v(16.43, 2.34) * mm});
            skPoint(sketch, "E43.start.orphan", {"position": v(17.63, 2.34) * mm});
            skLineSegment(sketch, "E44", {"start": v(14.43, 6.83) * mm, "end": v(16.43, 6.83) * mm});
            skLineSegment(sketch, "E45", {"start": v(16.43, 6.83) * mm, "end": v(16.43, 4.35) * mm});
            skLineSegment(sketch, "E46", {"start": v(16.43, 4.35) * mm, "end": v(14.43, 2.34) * mm});
            skSolve(sketch);
        }
        {
            var Q0;
            Q0 = qSketchRegion(id + "F11", true);
            var Q1;
            Q1=sQuery(id+"F0.wireOp",EDGE,"E2");
            revolve(context, id + "F12", {"operationType" : NewBodyOperationType.REMOVE, "surfaceOperationType" : NewSurfaceOperationType.NEW, "entities" : qUnion([Q0]), "axis" : qUnion([Q1]), "revolveType" : RevolveType.FULL, "oppositeDirection" : true});
        }
    });
